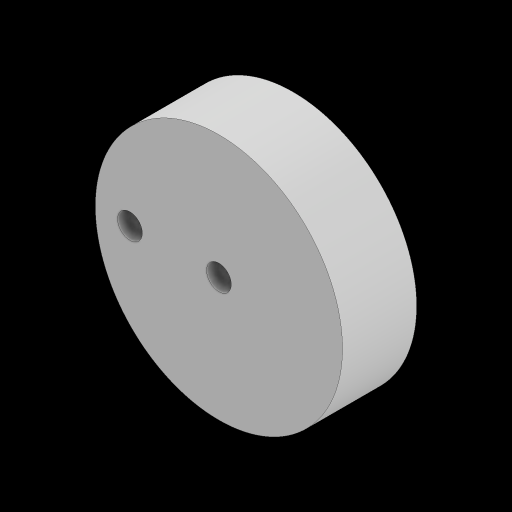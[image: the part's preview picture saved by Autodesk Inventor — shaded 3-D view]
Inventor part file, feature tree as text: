
AUTODESK INVENTOR PART (.ipt)
format: ipt  version: 2023 (Build 270158000, 158)  size: 97,792 bytes
history: native  units: mm
features: extrude x1, sketch x1
ambient origin geometry x8: Origin, YZ Plane, XZ Plane, XY Plane, X Axis, Y Axis, Z Axis, Center Point
bodies: Solid1 (feature_tree)
feature tree (2):
  extrude  "Extrusion1"  Depth=18.0mm
  sketch  "Sketch1"  dims[d0=50.0mm d1=5.0mm d2=15.0mm d3=0.0mm d4=5.0mm d5=18.0mm]
